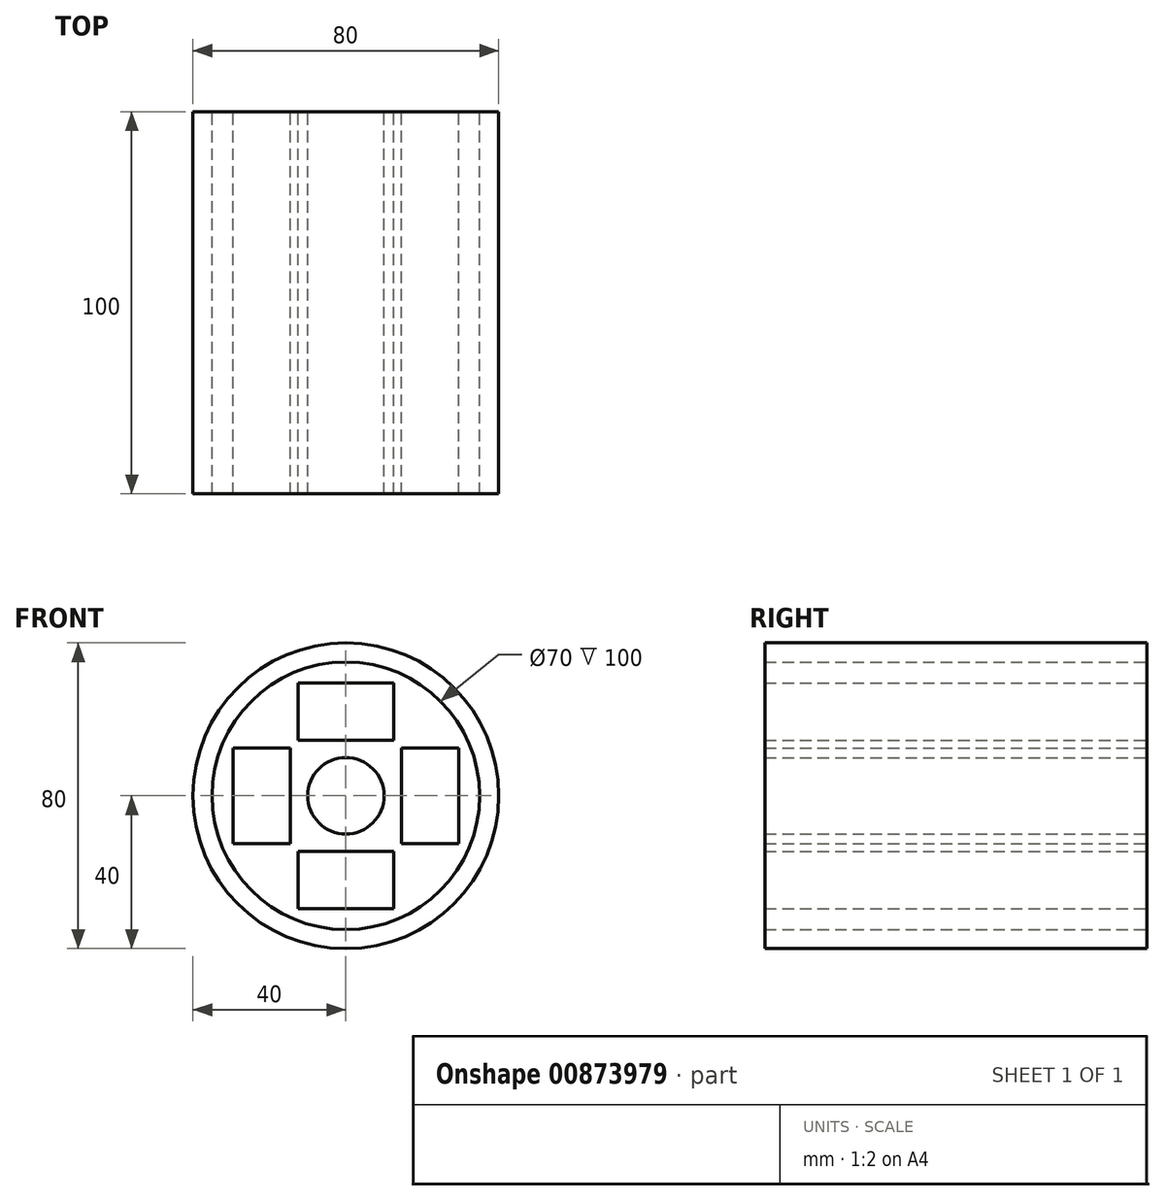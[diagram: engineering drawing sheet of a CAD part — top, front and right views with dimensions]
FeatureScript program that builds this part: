
annotation { "Feature Type Name" : "Feature", "Feature Type Description" : "" }
export const myFeature = defineFeature(function(context is Context, id is Id, definition is map)
    precondition{}
    {
        {
            var Q0;
            Q0=qCreatedBy(makeId("Front.planeOp"),FACE);
            var sketch = newSketch(context, id + "F0", { "sketchPlane" : qUnion([Q0])});
            skCircle(sketch, "E0", {"center": v(0, 0) * mm, "radius": 40 * mm});
            skCircle(sketch, "E1", {"center": v(0, 0) * mm, "radius": 10 * mm});
            skLineSegment(sketch, "E2.bottom", {"start": v(12.5, 14.5) * mm, "end": v(-12.5, 14.5) * mm});
            skLineSegment(sketch, "E2.top", {"start": v(12.5, 29.5) * mm, "end": v(-12.5, 29.5) * mm});
            skLineSegment(sketch, "E2.left", {"start": v(12.5, 14.5) * mm, "end": v(12.5, 29.5) * mm});
            skLineSegment(sketch, "E2.right", {"start": v(-12.5, 14.5) * mm, "end": v(-12.5, 29.5) * mm});
            skPoint(sketch, "E2.middle", {"position": v(0, 22) * mm});
            skCircle(sketch, "E3", {"center": v(0, 0) * mm, "radius": 35 * mm});
            skSolve(sketch);
        }
        {
            var Q0;
            Q0=makeQuery(id+"F0.imprint","IMPRINT",FACE,{"disambiguationData":[TD([[makeQuery(id+"F0.imprint","IMPRINT",EDGE,{"derivedFrom":sQuery(id+"F0.wireOp",EDGE,"E0")}),1.0]])]});
            var Q1;
            Q1=makeQuery(id+"F0.imprint","IMPRINT",FACE,{"disambiguationData":[TD([[makeQuery(id+"F0.imprint","IMPRINT",EDGE,{"derivedFrom":sQuery(id+"F0.wireOp",EDGE,"E1")}),1.0]])]});
            var Q2;
            Q2=makeQuery(id+"F0.imprint","IMPRINT",FACE,{"disambiguationData":[TD([[makeQuery(id+"F0.imprint","IMPRINT",EDGE,{"derivedFrom":sQuery(id+"F0.wireOp",EDGE,"E2.bottom")}),-1.0]])]});
            extrude(context, id + "F1", {"entities" : qUnion([Q0, Q1, Q2]), "endBound" : BoundingType.SYMMETRIC, "depth" : 100 * mm, "offsetDistance" : 25 * mm});
        }
        {
            var Q0;
            Q0=makeQuery(id+"F1.opExtrude","SWEPT_BODY",BODY,{"disambiguationData":[OSD([sQuery(id+"F0.wireOp",EDGE,"E2.bottom"),sQuery(id+"F0.wireOp",EDGE,"E2.top"),sQuery(id+"F0.wireOp",EDGE,"E2.left"),sQuery(id+"F0.wireOp",EDGE,"E2.right")])]});
            var Q1;
            Q1=makeQuery(id+"F1.opExtrude","SWEPT_FACE",FACE,{"disambiguationData":[OSD([sQuery(id+"F0.wireOp",EDGE,"E1")])]});
            circularPattern(context, id + "F2", {"entities" : qUnion([Q0]), "axis" : qUnion([Q1]), "angle" : 360 * degree, "instanceCount" : 4, "equalSpace" : true});
        }
    });
